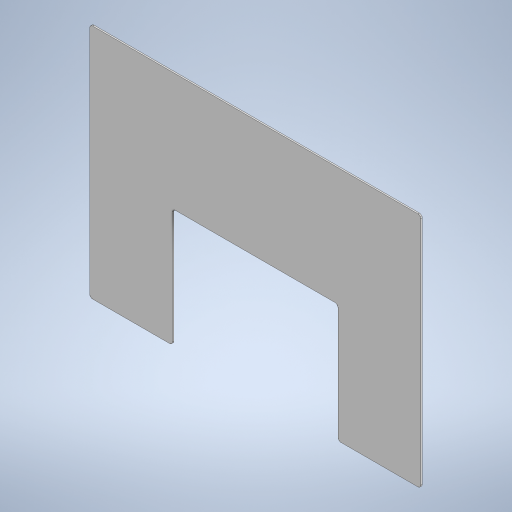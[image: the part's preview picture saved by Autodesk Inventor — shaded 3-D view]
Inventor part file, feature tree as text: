
AUTODESK INVENTOR PART (.ipt)
format: ipt  version: 2023 (Build 270158000, 158)  size: 231,424 bytes
history: native  units: in
note: dims shown in document units (in); Inventor stores cm internally (conversion verified against a paired STEP export)
features: fillet x8, extrude x1, sketch x1
ambient origin geometry x8: Origin, YZ Plane, XZ Plane, XY Plane, X Axis, Y Axis, Z Axis, Center Point
bodies: Solid1 (feature_tree)
feature tree (10):
  extrude  "Extrusion1"  Depth=10.0in
  fillet  "Fillet1"  Radius=0.0625in
  fillet  "Fillet2"  Radius=0.125in
  fillet  "Fillet3"  Radius=0.125in
  fillet  "Fillet4"  Radius=0.125in
  fillet  "Fillet5"  Radius=0.125in
  fillet  "Fillet6"  Radius=0.125in
  fillet  "Fillet7"  Radius=0.125in
  fillet  "Fillet8"  Radius=0.125in
  sketch  "Sketch1"  dims[d0=14.0in d1=10.0in d2=0.0625in d3=0.0in d4=0.125in d5=0.125in d6=0.125in d7=0.125in d8=0.125in d9=0.125in d10=0.125in d11=0.125in]
